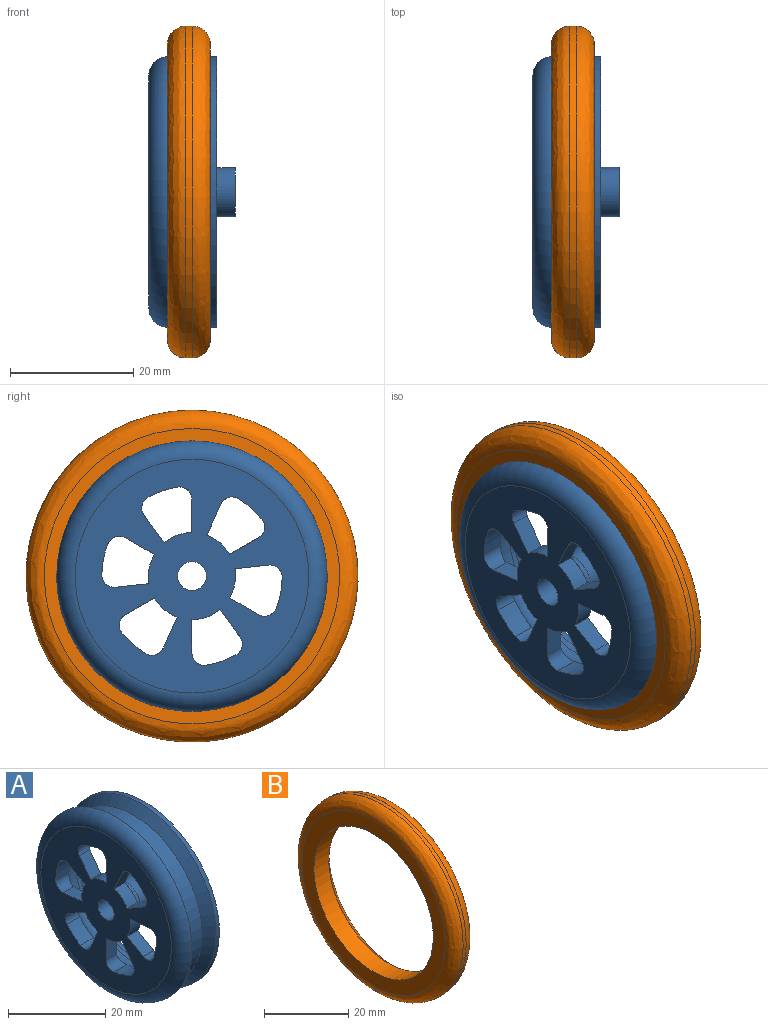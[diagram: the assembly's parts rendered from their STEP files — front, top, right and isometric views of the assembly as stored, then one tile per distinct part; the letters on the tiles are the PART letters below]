
ASSEMBLY  parts=2 mates=1
PART A: 51 faces, bbox 14x47.6x47.6 mm
  f0: plane 8x8mm, normal (1,0,0), area 32.9mm2, adj f1,f10
  f1: cylinder r=4mm len=8mm, axis (-1,0,0), area 201.1mm2, adj f0,f11
  f2: plane 24x23.74mm, normal (1,0,0), area 107.1mm2, adj f11,f12,f13,f14,f15,f17,f18,f19
  f3: cylinder r=17mm len=34mm, axis (-1,0,0), area 106.8mm2, adj f12,f47
  f4: plane 44x44mm, normal (1,0,0), area 386.4mm2, adj f5,f47
  f5: cylinder r=22mm len=44mm, axis (-1,0,0), area 138.2mm2, adj f4,f6
  f6: cone r=22mm half-angle=45deg, axis (1,0,0), area 373.2mm2, adj f5,f7
  f7: cylinder r=20mm len=40mm, axis (-1,0,0), area 628.3mm2, adj f6,f8
  f8: plane 44x44mm, normal (1,0,0), area 263.9mm2, adj f7,f50
  f9: plane 38x38mm, normal (-1,0,0), area 796.1mm2, adj f10,f13,f14,f15,f16,f17,f18,f19
  f10: cylinder r=2.35mm len=14mm, axis (-1,0,0), area 206.7mm2, adj f0,f9
  f11: torus R=7mm, axis (-1,0,0), area 150.7mm2, adj f1,f2
  f12: torus R=12mm, axis (-1,0,0), area 613.3mm2, adj f2,f3,f14,f15,f16,f18,f19,f20
  f13: cylinder r=7.08mm len=4.54mm, axis (-1,0,0), area 14.8mm2, adj f2,f9,f14,f15
  f14: plane 5.42x3.03mm, normal (0,1,0), area 16.3mm2, adj f2,f9,f12,f13,f46
  f15: plane 4.44x3.25mm, normal (0,-0.81,0.59), area 16.5mm2, adj f2,f9,f12,f13,f45
  f16: cylinder r=14.66mm len=4.84mm, axis (-1,0,0), area 19.4mm2, adj f9,f12,f45,f46
  f17: cylinder r=7.08mm len=4.75mm, axis (-1,0,0), area 14.8mm2, adj f2,f9,f18,f19
  f18: plane 4.7x3.03mm, normal (0,0.5,-0.87), area 16.3mm2, adj f2,f9,f12,f17,f49
  f19: plane 5.47x3.04mm, normal (0,0.11,0.99), area 16.5mm2, adj f2,f9,f12,f17,f48
  f20: cylinder r=14.66mm len=5.03mm, axis (-1,0,0), area 19.4mm2, adj f9,f12,f48,f49
  f21: cylinder r=7.08mm len=3.7mm, axis (-1,0,0), area 14.8mm2, adj f2,f9,f22,f23
  f22: plane 4.7x3.03mm, normal (0,0.5,0.87), area 16.3mm2, adj f2,f9,f12,f21,f44
  f23: plane 5.04x3.04mm, normal (0,-0.92,-0.4), area 16.5mm2, adj f2,f9,f12,f21,f37
  f24: cylinder r=14.66mm len=3.87mm, axis (-1,0,0), area 19.4mm2, adj f9,f12,f37,f44
  f25: cylinder r=7.08mm len=4.75mm, axis (-1,0,0), area 14.8mm2, adj f2,f9,f26,f27
  f26: plane 4.7x3.03mm, normal (0,-0.5,0.87), area 16.3mm2, adj f2,f9,f12,f25,f43
  f27: plane 5.47x3.04mm, normal (0,-0.11,-0.99), area 16.5mm2, adj f2,f9,f12,f25,f42
  f28: cylinder r=14.66mm len=5.03mm, axis (-1,0,0), area 19.4mm2, adj f9,f12,f42,f43
  f29: cylinder r=7.08mm len=4.54mm, axis (-1,0,0), area 14.8mm2, adj f2,f9,f30,f31
  f30: plane 5.42x3.03mm, normal (0,-1,0), area 16.3mm2, adj f2,f9,f12,f29,f41
  f31: plane 4.44x3.25mm, normal (0,0.81,-0.59), area 16.5mm2, adj f2,f9,f12,f29,f40
  f32: cylinder r=14.66mm len=4.84mm, axis (-1,0,0), area 19.4mm2, adj f9,f12,f40,f41
  f33: cylinder r=7.08mm len=3.7mm, axis (-1,0,0), area 14.8mm2, adj f2,f9,f34,f35
  f34: plane 4.7x3.03mm, normal (0,-0.5,-0.87), area 16.3mm2, adj f2,f9,f12,f33,f39
  f35: plane 5.04x3.04mm, normal (0,0.92,0.4), area 16.5mm2, adj f2,f9,f12,f33,f38
  f36: cylinder r=14.66mm len=3.87mm, axis (-1,0,0), area 19.4mm2, adj f9,f12,f38,f39
  f37: cylinder r=2mm len=3.77mm, axis (-1,0,0), area 11.6mm2, adj f9,f12,f23,f24
  f38: cylinder r=2mm len=3.77mm, axis (-1,0,0), area 11.6mm2, adj f9,f12,f35,f36
  f39: cylinder r=2mm len=3.77mm, axis (-1,0,0), area 11.8mm2, adj f9,f12,f34,f36
  f40: cylinder r=2mm len=3.77mm, axis (-1,0,0), area 11.6mm2, adj f9,f12,f31,f32
  f41: cylinder r=2mm len=3.77mm, axis (-1,0,0), area 11.8mm2, adj f9,f12,f30,f32
  f42: cylinder r=2mm len=3.77mm, axis (-1,0,0), area 11.6mm2, adj f9,f12,f27,f28
  f43: cylinder r=2mm len=3.77mm, axis (-1,0,0), area 11.8mm2, adj f9,f12,f26,f28
  f44: cylinder r=2mm len=3.77mm, axis (-1,0,0), area 11.8mm2, adj f9,f12,f22,f24
  f45: cylinder r=2mm len=3.77mm, axis (-1,0,0), area 11.6mm2, adj f9,f12,f15,f16
  f46: cylinder r=2mm len=3.77mm, axis (-1,0,0), area 11.8mm2, adj f9,f12,f14,f16
  f47: torus R=19mm, axis (-1,0,0), area 349.9mm2, adj f3,f4
  f48: cylinder r=2mm len=3.77mm, axis (-1,0,0), area 11.6mm2, adj f9,f12,f19,f20
  f49: cylinder r=2mm len=3.77mm, axis (-1,0,0), area 11.8mm2, adj f9,f12,f18,f20
  f50: torus R=19mm, axis (-1,0,0), area 619.1mm2, adj f8,f9
PART B: 7 faces, bbox 7x54x54 mm
  f0: plane 48x48mm, normal (1,0,0), area 289mm2, adj f1,f6
  f1: revolved ~54x54mm, area 767.1mm2, adj f0,f2
  f2: cylinder r=27mm len=54mm, axis (-1,0,0), area 169.6mm2, adj f1,f3
  f3: revolved ~54x54mm, area 767.1mm2, adj f2,f4
  f4: plane 48x48mm, normal (-1,0,0), area 552.9mm2, adj f3,f5
  f5: cylinder r=20mm len=40mm, axis (-1,0,0), area 628.3mm2, adj f4,f6
  f6: revolved ~44x44mm, area 746.4mm2, adj f0,f5
PLACE A t=(-15.65,-1.28,1.3)mm
PLACE B t=(-12.65,18.72,1.6)mm
MATE slider B.f2 <-> A.f10  axis (-1,0,0) through (-7.65,-1.28,1.3)mm
